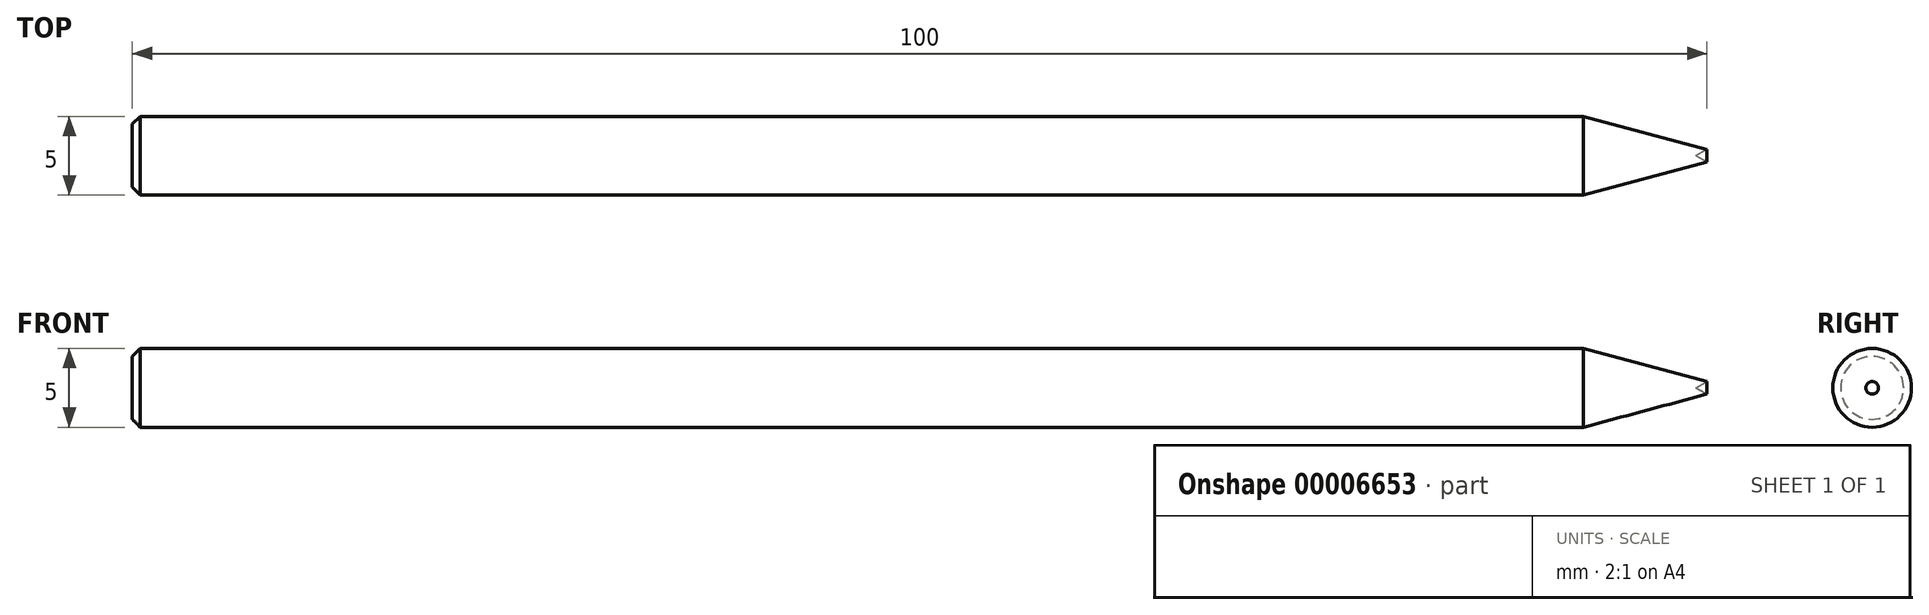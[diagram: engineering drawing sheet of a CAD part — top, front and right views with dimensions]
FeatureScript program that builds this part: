
annotation { "Feature Type Name" : "Feature", "Feature Type Description" : "" }
export const myFeature = defineFeature(function(context is Context, id is Id, definition is map)
    precondition{}
    {
        {
            var Q0;
            Q0=qCreatedBy(makeId("Right.planeOp"),FACE);
            var sketch = newSketch(context, id + "F0", { "sketchPlane" : qUnion([Q0])});
            skCircle(sketch, "E0", {"center": v(0, 0) * mm, "radius": 2.5 * mm});
            skSolve(sketch);
        }
        {
            var Q0;
            Q0 = qSketchRegion(id + "F0", true);
            extrude(context, id + "F1", {"entities" : qUnion([Q0]), "depth" : 100 * mm});
        }
        {
            var Q0;
            Q0=qCreatedBy(makeId("Front.planeOp"),FACE);
            var sketch = newSketch(context, id + "F2", { "sketchPlane" : qUnion([Q0])});
            skLineSegment(sketch, "E1.0.0", {"start": v(100, 2.5) * mm, "end": v(100, -2.5) * mm, "construction": true});
            skLineSegment(sketch, "E2", {"start": v(100, 2.5) * mm, "end": v(92.16, 2.5) * mm});
            skLineSegment(sketch, "E3", {"start": v(92.16, 2.5) * mm, "end": v(100, 0.4) * mm});
            skLineSegment(sketch, "E4", {"start": v(100, 0.4) * mm, "end": v(99.3, 0) * mm});
            skLineSegment(sketch, "E5", {"start": v(99.3, 0) * mm, "end": v(100, 0) * mm});
            skLineSegment(sketch, "E6", {"start": v(100, 0) * mm, "end": v(100, 2.5) * mm});
            skSolve(sketch);
        }
        {
            var Q0;
            Q0 = qSketchRegion(id + "F2", true);
            var Q1;
            Q1=sQuery(id+"F2.wireOp",EDGE,"E2");
            var Q2;
            Q2=sQuery(id+"F2.wireOp",EDGE,"E5");
            revolve(context, id + "F3", {"operationType" : NewBodyOperationType.REMOVE, "entities" : qUnion([Q0]), "surfaceEntities" : qUnion([Q1]), "axis" : qUnion([Q2]), "revolveType" : RevolveType.FULL, "oppositeDirection" : true});
        }
        {
            var Q0;
            Q0=makeQuery(id+"F1.opExtrude","CAP_EDGE",EDGE,{"disambiguationData":[OSD([sQuery(id+"F0.wireOp",EDGE,"E0")])],"isStart":true});
            chamfer(context, id + "F4", {"entities" : qUnion([Q0]), "width" : .5 * mm, "tangentPropagation" : true});
        }
    });
